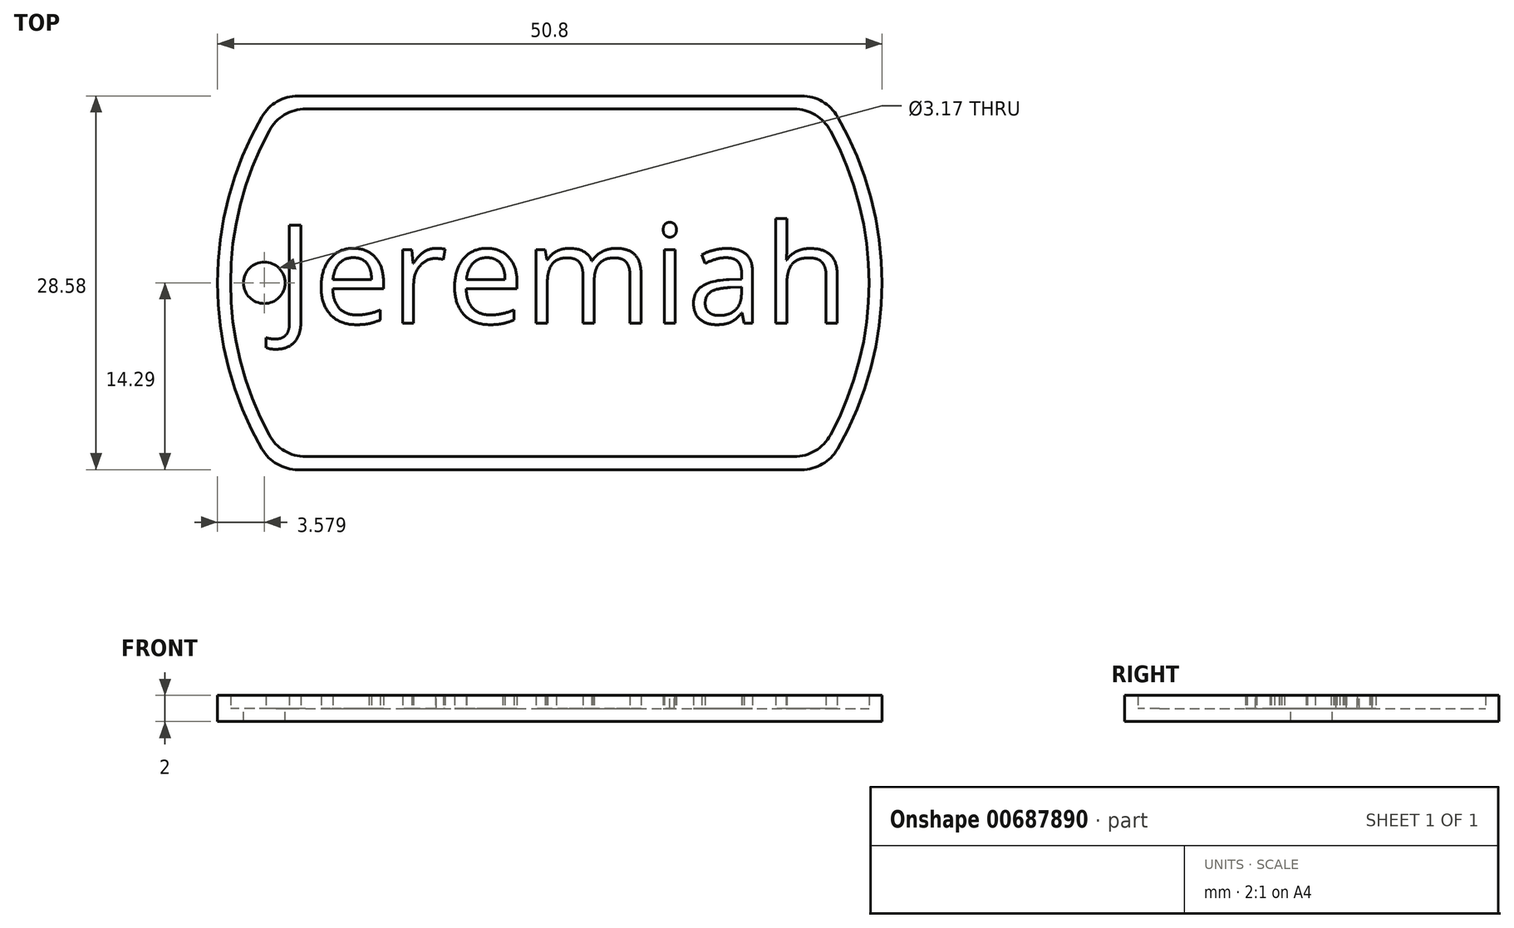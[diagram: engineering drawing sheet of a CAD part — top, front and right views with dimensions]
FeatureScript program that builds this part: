
annotation { "Feature Type Name" : "Feature", "Feature Type Description" : "" }
export const myFeature = defineFeature(function(context is Context, id is Id, definition is map)
    precondition{}
    {
        {
            var Q0;
            Q0=qCreatedBy(makeId("Top.planeOp"),FACE);
            var sketch = newSketch(context, id + "F0", { "sketchPlane" : qUnion([Q0])});
            skArc(sketch, "E0", {"start": v(-22, 12.7) * mm, "mid": v(-25.4, 0) * mm, "end": v(-22, -12.7) * mm});
            skLineSegment(sketch, "E1.top", {"start": v(-19.25, -14.29) * mm, "end": v(19.25, -14.29) * mm});
            skArc(sketch, "E2.trimOffspring", {"start": v(22, -12.7) * mm, "mid": v(25.4, 0) * mm, "end": v(22, 12.7) * mm});
            skLineSegment(sketch, "E3", {"start": v(-19.25, 14.29) * mm, "end": v(19.25, 14.29) * mm});
            skPoint(sketch, "E4.visualSharp", {"position": v(-21, 14.29) * mm});
            skArc(sketch, "E4.filletArc", {"start": v(-19.25, 14.29) * mm, "mid": v(-20.83, 13.86) * mm, "end": v(-22, 12.7) * mm});
            skPoint(sketch, "E5.visualSharp", {"position": v(21, 14.29) * mm});
            skArc(sketch, "E5.filletArc", {"start": v(22, 12.7) * mm, "mid": v(20.83, 13.86) * mm, "end": v(19.25, 14.29) * mm});
            skPoint(sketch, "E6.visualSharp", {"position": v(21, -14.29) * mm});
            skArc(sketch, "E6.filletArc", {"start": v(19.25, -14.29) * mm, "mid": v(20.83, -13.86) * mm, "end": v(22, -12.7) * mm});
            skPoint(sketch, "E7.visualSharp", {"position": v(-21, -14.29) * mm});
            skArc(sketch, "E7.filletArc", {"start": v(-22, -12.7) * mm, "mid": v(-20.83, -13.86) * mm, "end": v(-19.25, -14.29) * mm});
            skSolve(sketch);
        }
        {
            var Q0;
            Q0=makeQuery(id+"F0.imprint","IMPRINT",FACE,{"disambiguationData":[TD([[makeQuery(id+"F0.imprint","IMPRINT",EDGE,{"derivedFrom":sQuery(id+"F0.wireOp",EDGE,"E0")}),1.0]])]});
            extrude(context, id + "F1", {"entities" : qUnion([Q0]), "depth" : 1 * mm, "offsetDistance" : 25.4 * mm});
        }
        {
            var Q0;
            Q0=makeQuery(id+"F1.opExtrude","CAP_FACE",FACE,{"disambiguationData":[OSD([sQuery(id+"F0.wireOp",EDGE,"E0"),sQuery(id+"F0.wireOp",EDGE,"E1.top"),sQuery(id+"F0.wireOp",EDGE,"E2.trimOffspring"),sQuery(id+"F0.wireOp",EDGE,"E3"),sQuery(id+"F0.wireOp",EDGE,"E4.filletArc"),sQuery(id+"F0.wireOp",EDGE,"E5.filletArc"),sQuery(id+"F0.wireOp",EDGE,"E6.filletArc"),sQuery(id+"F0.wireOp",EDGE,"E7.filletArc")])],"isStart":false});
            var sketch = newSketch(context, id + "F2", { "sketchPlane" : qUnion([Q0])});
            skLineSegment(sketch, "E8.0", {"start": v(-18.66, 13.29) * mm, "end": v(18.66, 13.29) * mm});
            skArc(sketch, "E8.1", {"start": v(-21.45, 11.63) * mm, "mid": v(-24.4, 0) * mm, "end": v(-21.45, -11.63) * mm});
            skLineSegment(sketch, "E8.2", {"start": v(-18.66, -13.29) * mm, "end": v(18.66, -13.29) * mm});
            skArc(sketch, "E8.3", {"start": v(21.45, -11.63) * mm, "mid": v(24.4, 0) * mm, "end": v(21.45, 11.63) * mm});
            skPoint(sketch, "E9.visualSharp", {"position": v(-20.46, 13.29) * mm});
            skArc(sketch, "E9.filletArc", {"start": v(-18.66, 13.29) * mm, "mid": v(-20.29, 12.84) * mm, "end": v(-21.45, 11.63) * mm});
            skPoint(sketch, "E10.visualSharp", {"position": v(20.46, 13.29) * mm});
            skArc(sketch, "E10.filletArc", {"start": v(21.45, 11.63) * mm, "mid": v(20.29, 12.84) * mm, "end": v(18.66, 13.29) * mm});
            skPoint(sketch, "E11.visualSharp", {"position": v(20.46, -13.29) * mm});
            skArc(sketch, "E11.filletArc", {"start": v(18.66, -13.29) * mm, "mid": v(20.29, -12.84) * mm, "end": v(21.45, -11.63) * mm});
            skPoint(sketch, "E12.visualSharp", {"position": v(-20.46, -13.29) * mm});
            skArc(sketch, "E12.filletArc", {"start": v(-21.45, -11.63) * mm, "mid": v(-20.29, -12.84) * mm, "end": v(-18.66, -13.29) * mm});
            skLineSegment(sketch, "E13.0", {"start": v(-19.25, 14.29) * mm, "end": v(19.25, 14.29) * mm});
            skArc(sketch, "E13.1", {"start": v(-22, 12.7) * mm, "mid": v(-25.4, 0) * mm, "end": v(-22, -12.7) * mm});
            skLineSegment(sketch, "E13.2", {"start": v(-19.25, -14.29) * mm, "end": v(19.25, -14.29) * mm});
            skArc(sketch, "E13.3", {"start": v(22, -12.7) * mm, "mid": v(25.4, 0) * mm, "end": v(22, 12.7) * mm});
            skPoint(sketch, "E14.visualSharp", {"position": v(-21, -14.29) * mm});
            skArc(sketch, "E14.filletArc", {"start": v(-22, -12.7) * mm, "mid": v(-20.83, -13.86) * mm, "end": v(-19.25, -14.29) * mm});
            skPoint(sketch, "E15.visualSharp", {"position": v(21, -14.29) * mm});
            skArc(sketch, "E15.filletArc", {"start": v(19.25, -14.29) * mm, "mid": v(20.83, -13.86) * mm, "end": v(22, -12.7) * mm});
            skPoint(sketch, "E16.visualSharp", {"position": v(21, 14.29) * mm});
            skArc(sketch, "E16.filletArc", {"start": v(22, 12.7) * mm, "mid": v(20.83, 13.86) * mm, "end": v(19.25, 14.29) * mm});
            skPoint(sketch, "E17.visualSharp", {"position": v(-21, 14.29) * mm});
            skArc(sketch, "E17.filletArc", {"start": v(-19.25, 14.29) * mm, "mid": v(-20.83, 13.86) * mm, "end": v(-22, 12.7) * mm});
            skSolve(sketch);
        }
        {
            var Q0;
            Q0=makeQuery(id+"F2.imprint","IMPRINT",FACE,{"disambiguationData":[TD([[makeQuery(id+"F2.imprint","IMPRINT",EDGE,{"derivedFrom":sQuery(id+"F2.wireOp",EDGE,"E8.0")}),1.0]])]});
            extrude(context, id + "F3", {"entities" : qUnion([Q0]), "operationType" : NewBodyOperationType.ADD, "depth" : 1 * mm, "offsetDistance" : 25.4 * mm});
        }
        {
            var Q0;
            Q0=makeQuery(id+"F1.opExtrude","CAP_FACE",FACE,{"disambiguationData":[OSD([sQuery(id+"F0.wireOp",EDGE,"E0"),sQuery(id+"F0.wireOp",EDGE,"E1.top"),sQuery(id+"F0.wireOp",EDGE,"E2.trimOffspring"),sQuery(id+"F0.wireOp",EDGE,"E3"),sQuery(id+"F0.wireOp",EDGE,"E4.filletArc"),sQuery(id+"F0.wireOp",EDGE,"E5.filletArc"),sQuery(id+"F0.wireOp",EDGE,"E6.filletArc"),sQuery(id+"F0.wireOp",EDGE,"E7.filletArc")])],"isStart":false});
            var sketch = newSketch(context, id + "F4", { "sketchPlane" : qUnion([Q0])});
            skCircle(sketch, "E18", {"center": v(-21.82, 0) * mm, "radius": 1.59 * mm});
            skSolve(sketch);
        }
        {
            var Q0;
            Q0=makeQuery(id+"F4.imprint","IMPRINT",FACE,{"disambiguationData":[TD([[makeQuery(id+"F4.imprint","IMPRINT",EDGE,{"derivedFrom":sQuery(id+"F4.wireOp",EDGE,"E18")}),1.0]])]});
            extrude(context, id + "F5", {"entities" : qUnion([Q0]), "operationType" : NewBodyOperationType.REMOVE, "oppositeDirection" : true, "depth" : 1 * mm, "offsetDistance" : 25.4 * mm});
        }
        {
            var Q0;
            Q0=makeQuery(id+"F2.imprint","IMPRINT",FACE,{"disambiguationData":[TD([[makeQuery(id+"F2.imprint","IMPRINT",EDGE,{"derivedFrom":sQuery(id+"F2.wireOp",EDGE,"E8.0")}),-1.0]])]});
            var sketch = newSketch(context, id + "F6", { "sketchPlane" : qUnion([Q0])});
            skText(sketch, "E19", { "text": "Jeremiah", "fontName": "OpenSans-Regular.ttf"});
            const initialGuessF6  = {"E19": [-0.02088, -0.0031, 1, 0, 0.00758]};
            skSetInitialGuess(sketch, initialGuessF6);
            skSolve(sketch);
        }
        {
            var Q0;
            Q0 = qSketchRegion(id + "F6", true);
            extrude(context, id + "F7", {"entities" : qUnion([Q0]), "operationType" : NewBodyOperationType.ADD, "depth" : 1 * mm, "offsetDistance" : 25.4 * mm});
        }
    });
